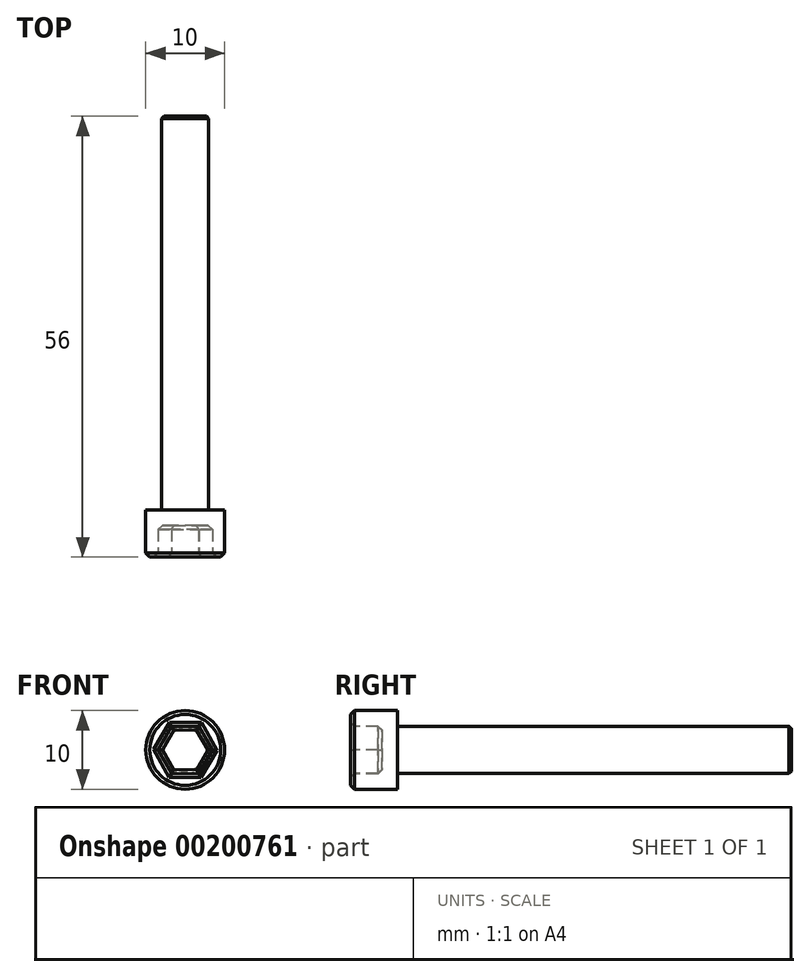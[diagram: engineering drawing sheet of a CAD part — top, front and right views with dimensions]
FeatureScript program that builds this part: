
annotation { "Feature Type Name" : "Feature", "Feature Type Description" : "" }
export const myFeature = defineFeature(function(context is Context, id is Id, definition is map)
    precondition{}
    {
        {
            var Q0;
            Q0=qCreatedBy(makeId("Front.planeOp"),FACE);
            var sketch = newSketch(context, id + "F0", { "sketchPlane" : qUnion([Q0])});
            skCircle(sketch, "E0", {"center": v(0, 0) * mm, "radius": 5 * mm});
            skSolve(sketch);
        }
        {
            var Q0;
            Q0=qSketchRegion(id+"F0",true);
            extrude(context, id + "F1", {"entities" : qUnion([Q0]), "depth" : 6 * mm});
        }
        {
            var Q0;
            Q0=makeQuery(id+"F1.opExtrude","CAP_FACE",FACE,{"disambiguationData":[OSD([sQuery(id+"F0.wireOp",EDGE,"E0")])],"isStart":false});
            var sketch = newSketch(context, id + "F2", { "sketchPlane" : qUnion([Q0])});
            skCircle(sketch, "E1.cCircle", {"center": v(0, 0) * mm, "radius": 3.46 * mm, "construction": true});
            skLineSegment(sketch, "E1.0", {"start": v(1.76, 2.98) * mm, "end": v(3.46, -0.03) * mm});
            skLineSegment(sketch, "E1.1", {"start": v(3.46, -0.03) * mm, "end": v(1.7, -3.01) * mm});
            skLineSegment(sketch, "E1.2", {"start": v(1.7, -3.01) * mm, "end": v(-1.76, -2.98) * mm});
            skLineSegment(sketch, "E1.3", {"start": v(-1.76, -2.98) * mm, "end": v(-3.46, 0.03) * mm});
            skLineSegment(sketch, "E1.4", {"start": v(-3.46, 0.03) * mm, "end": v(-1.7, 3.01) * mm});
            skLineSegment(sketch, "E1.5", {"start": v(-1.7, 3.01) * mm, "end": v(1.76, 2.98) * mm});
            skSolve(sketch);
        }
        {
            var Q0;
            Q0=qSketchRegion(id+"F2",true);
            extrude(context, id + "F3", {"entities" : qUnion([Q0]), "operationType" : NewBodyOperationType.REMOVE, "oppositeDirection" : true, "depth" : 4 * mm});
        }
        {
            var Q0;
            Q0=makeQuery(id+"F1.opExtrude","CAP_EDGE",EDGE,{"disambiguationData":[OSD([sQuery(id+"F0.wireOp",EDGE,"E0")])],"isStart":false});
            var Q1;
            Q1=makeQuery(id+"F3.boolean.opBoolean","COPY",FACE,{"derivedFrom":makeQuery(id+"F3.opExtrude","CAP_FACE",FACE,{"disambiguationData":[OSD([sQuery(id+"F2.wireOp",EDGE,"E1.0"),sQuery(id+"F2.wireOp",EDGE,"E1.1"),sQuery(id+"F2.wireOp",EDGE,"E1.2"),sQuery(id+"F2.wireOp",EDGE,"E1.3"),sQuery(id+"F2.wireOp",EDGE,"E1.4"),sQuery(id+"F2.wireOp",EDGE,"E1.5")])],"isStart":false})});
            var Q2;
            Q2=makeQuery(id+"F3.boolean.opBoolean","COPY",EDGE,{"derivedFrom":makeQuery(id+"F3.opExtrude","CAP_EDGE",EDGE,{"disambiguationData":[OSD([sQuery(id+"F2.wireOp",EDGE,"E1.4")])],"isStart":true})});
            var Q3;
            Q3=makeQuery(id+"F3.boolean.opBoolean","COPY",EDGE,{"derivedFrom":makeQuery(id+"F3.opExtrude","CAP_EDGE",EDGE,{"disambiguationData":[OSD([sQuery(id+"F2.wireOp",EDGE,"E1.3")])],"isStart":true})});
            var Q4;
            Q4=makeQuery(id+"F3.boolean.opBoolean","COPY",EDGE,{"derivedFrom":makeQuery(id+"F3.opExtrude","CAP_EDGE",EDGE,{"disambiguationData":[OSD([sQuery(id+"F2.wireOp",EDGE,"E1.5")])],"isStart":true})});
            var Q5;
            Q5=makeQuery(id+"F1.opExtrude","CAP_FACE",FACE,{"disambiguationData":[OSD([sQuery(id+"F0.wireOp",EDGE,"E0")])],"isStart":false});
            chamfer(context, id + "F6", {"entities" : qUnion([Q0, Q1, Q2, Q3, Q4, Q5]), "width" : 0.5 * mm, "tangentPropagation" : true});
        }
        {
            var Q0;
            Q0=makeQuery(id+"F1.opExtrude","CAP_FACE",FACE,{"disambiguationData":[OSD([sQuery(id+"F0.wireOp",EDGE,"E0")])],"isStart":true});
            var sketch = newSketch(context, id + "F7", { "sketchPlane" : qUnion([Q0])});
            skCircle(sketch, "E2", {"center": v(0, 0) * mm, "radius": 3 * mm});
            skSolve(sketch);
        }
        {
            var Q0;
            Q0=qSketchRegion(id+"F7",true);
            extrude(context, id + "F4", {"entities" : qUnion([Q0]), "operationType" : NewBodyOperationType.ADD, "depth" : 50 * mm});
        }
        {
            var Q0;
            Q0=makeQuery(id+"F4.opExtrude","CAP_EDGE",EDGE,{"disambiguationData":[OSD([sQuery(id+"F7.wireOp",EDGE,"E2")])],"isStart":false});
            chamfer(context, id + "F5", {"entities" : qUnion([Q0]), "width" : 0.3 * mm, "tangentPropagation" : true});
        }
    });
